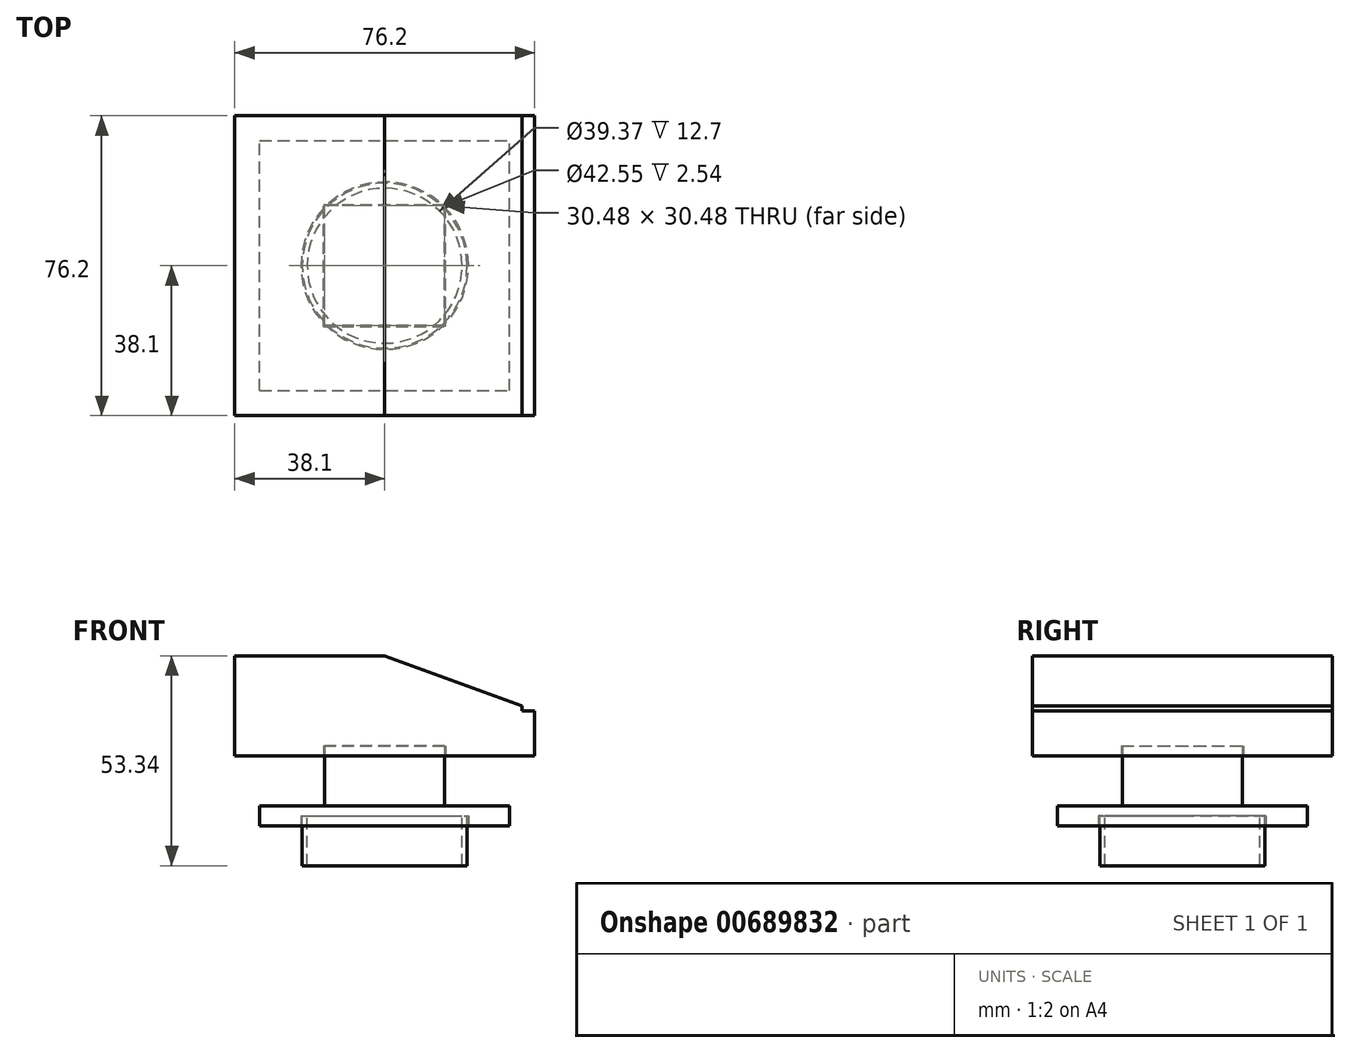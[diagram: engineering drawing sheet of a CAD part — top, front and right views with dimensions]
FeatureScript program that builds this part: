
annotation { "Feature Type Name" : "Feature", "Feature Type Description" : "" }
export const myFeature = defineFeature(function(context is Context, id is Id, definition is map)
    precondition{}
    {
        {
            var Q0;
            Q0=qCreatedBy(makeId("Front.planeOp"),FACE);
            var sketch = newSketch(context, id + "F0", { "sketchPlane" : qUnion([Q0])});
            skLineSegment(sketch, "E0.bottom", {"start": v(-38.1, 0) * mm, "end": v(38.1, 0) * mm});
            skLineSegment(sketch, "E0.top", {"start": v(-38.1, -25.4) * mm, "end": v(38.1, -25.4) * mm});
            skLineSegment(sketch, "E0.left", {"start": v(-38.1, 0) * mm, "end": v(-38.1, -25.4) * mm});
            skLineSegment(sketch, "E0.right", {"start": v(38.1, 0) * mm, "end": v(38.1, -25.4) * mm});
            skSolve(sketch);
        }
        {
            var Q0;
            Q0=qSketchRegion(id+"F0",true);
            extrude(context, id + "F1", {"entities" : qUnion([Q0]), "endBound" : BoundingType.SYMMETRIC, "depth" : 76.2 * mm, "offsetDistance" : 25.4 * mm});
        }
        {
            var Q0;
            Q0=qCreatedBy(makeId("Front.planeOp"),FACE);
            var sketch = newSketch(context, id + "F2", { "sketchPlane" : qUnion([Q0])});
            skLineSegment(sketch, "E1", {"start": v(0, 0) * mm, "end": v(34.93, -12.7) * mm});
            skLineSegment(sketch, "E2", {"start": v(34.93, -12.7) * mm, "end": v(34.93, -13.99) * mm});
            skLineSegment(sketch, "E3", {"start": v(34.93, -13.99) * mm, "end": v(38.1, -13.99) * mm});
            skLineSegment(sketch, "E4", {"start": v(38.1, -13.99) * mm, "end": v(38.1, -25.4) * mm});
            skLineSegment(sketch, "E5", {"start": v(38.1, -25.4) * mm, "end": v(53.54, -25.4) * mm});
            skLineSegment(sketch, "E6", {"start": v(53.54, -25.4) * mm, "end": v(53.54, 0) * mm});
            skLineSegment(sketch, "E7", {"start": v(53.54, 0) * mm, "end": v(0, 0) * mm});
            skSolve(sketch);
        }
        {
            var Q0;
            Q0=qSketchRegion(id+"F2",true);
            extrude(context, id + "F3", {"entities" : qUnion([Q0]), "operationType" : NewBodyOperationType.REMOVE, "endBound" : BoundingType.SYMMETRIC, "oppositeDirection" : true, "depth" : 76.2 * mm, "offsetDistance" : 25.4 * mm});
        }
        {
            var Q0;
            Q0=qCreatedBy(makeId("Front.planeOp"),FACE);
            var sketch = newSketch(context, id + "F4", { "sketchPlane" : qUnion([Q0])});
            skLineSegment(sketch, "E8", {"start": v(0, -1.4) * mm, "end": v(0, -17.06) * mm});
            skSolve(sketch);
        }
        {
            var Q0;
            Q0=makeQuery(id+"F1.opExtrude","SWEPT_FACE",FACE,{"disambiguationData":[OSD([sQuery(id+"F0.wireOp",EDGE,"E0.top")])]});
            var sketch = newSketch(context, id + "F5", { "sketchPlane" : qUnion([Q0])});
            skLineSegment(sketch, "E9.bottom", {"start": v(-15.5, 15.5) * mm, "end": v(15.5, 15.5) * mm});
            skLineSegment(sketch, "E9.top", {"start": v(-15.5, -15.5) * mm, "end": v(15.5, -15.5) * mm});
            skLineSegment(sketch, "E9.left", {"start": v(-15.5, 15.5) * mm, "end": v(-15.5, -15.5) * mm});
            skLineSegment(sketch, "E9.right", {"start": v(15.5, 15.5) * mm, "end": v(15.5, -15.5) * mm});
            skSolve(sketch);
        }
        {
            var Q0;
            Q0=qSketchRegion(id+"F5",true);
            extrude(context, id + "F6", {"entities" : qUnion([Q0]), "operationType" : NewBodyOperationType.REMOVE, "oppositeDirection" : true, "depth" : 2.54 * mm, "offsetDistance" : 25.4 * mm});
        }
        {
            var Q0;
            Q0=qCreatedBy(makeId("Front.planeOp"),FACE);
            var sketch = newSketch(context, id + "F7", { "sketchPlane" : qUnion([Q0])});
            skLineSegment(sketch, "E10.bottom", {"start": v(-31.75, -38.1) * mm, "end": v(31.75, -38.1) * mm});
            skLineSegment(sketch, "E10.top", {"start": v(-31.75, -43.18) * mm, "end": v(31.75, -43.18) * mm});
            skLineSegment(sketch, "E10.left", {"start": v(-31.75, -38.1) * mm, "end": v(-31.75, -43.18) * mm});
            skLineSegment(sketch, "E10.right", {"start": v(31.75, -38.1) * mm, "end": v(31.75, -43.18) * mm});
            skSolve(sketch);
        }
        {
            var Q0;
            Q0=qSketchRegion(id+"F7",true);
            extrude(context, id + "F8", {"entities" : qUnion([Q0]), "endBound" : BoundingType.SYMMETRIC, "depth" : 63.5 * mm, "offsetDistance" : 25.4 * mm});
        }
        {
            var Q0;
            Q0=makeQuery(id+"F8.opExtrude","SWEPT_FACE",FACE,{"disambiguationData":[OSD([sQuery(id+"F7.wireOp",EDGE,"E10.bottom")])]});
            var sketch = newSketch(context, id + "F9", { "sketchPlane" : qUnion([Q0])});
            skLineSegment(sketch, "E11.bottom", {"start": v(-15.24, 15.24) * mm, "end": v(15.24, 15.24) * mm});
            skLineSegment(sketch, "E11.top", {"start": v(-15.24, -15.24) * mm, "end": v(15.24, -15.24) * mm});
            skLineSegment(sketch, "E11.left", {"start": v(-15.24, 15.24) * mm, "end": v(-15.24, -15.24) * mm});
            skLineSegment(sketch, "E11.right", {"start": v(15.24, 15.24) * mm, "end": v(15.24, -15.24) * mm});
            skSolve(sketch);
        }
        {
            var Q0;
            Q0=qSketchRegion(id+"F9",true);
            var Q1;
            Q1=makeQuery(id+"F6.boolean.opBoolean","COPY",FACE,{"derivedFrom":makeQuery(id+"F6.opExtrude","CAP_FACE",FACE,{"disambiguationData":[OSD([sQuery(id+"F5.wireOp",EDGE,"E9.bottom"),sQuery(id+"F5.wireOp",EDGE,"E9.top"),sQuery(id+"F5.wireOp",EDGE,"E9.left"),sQuery(id+"F5.wireOp",EDGE,"E9.right")])],"isStart":false})});
            extrude(context, id + "F10", {"entities" : qUnion([Q0]), "operationType" : NewBodyOperationType.ADD, "endBound" : BoundingType.UP_TO_SURFACE, "depth" : 25.4 * mm, "endBoundEntityFace" : qUnion([Q1]), "offsetDistance" : 25.4 * mm});
        }
        {
            var Q0;
            Q0=makeQuery(id+"F8.opExtrude","SWEPT_FACE",FACE,{"disambiguationData":[OSD([sQuery(id+"F7.wireOp",EDGE,"E10.top")])]});
            var sketch = newSketch(context, id + "F11", { "sketchPlane" : qUnion([Q0])});
            skCircle(sketch, "E12", {"center": v(0, 0) * mm, "radius": 21.27 * mm});
            skSolve(sketch);
        }
        {
            var Q0;
            Q0=qSketchRegion(id+"F11",true);
            extrude(context, id + "F12", {"entities" : qUnion([Q0]), "operationType" : NewBodyOperationType.REMOVE, "oppositeDirection" : true, "depth" : 2.54 * mm, "offsetDistance" : 25.4 * mm});
        }
        {
            var Q0;
            Q0=makeQuery(id+"F12.boolean.opBoolean","COPY",FACE,{"derivedFrom":makeQuery(id+"F12.opExtrude","CAP_FACE",FACE,{"disambiguationData":[OSD([sQuery(id+"F11.wireOp",EDGE,"E12")])],"isStart":false})});
            var sketch = newSketch(context, id + "F13", { "sketchPlane" : qUnion([Q0])});
            skCircle(sketch, "E13", {"center": v(0, 0) * mm, "radius": 20.96 * mm});
            skCircle(sketch, "E14", {"center": v(0, 0) * mm, "radius": 19.69 * mm});
            skSolve(sketch);
        }
        {
            var Q0;
            Q0=qSketchRegion(id+"F13",true);
            extrude(context, id + "F14", {"entities" : qUnion([Q0]), "depth" : 12.7 * mm, "offsetDistance" : 25.4 * mm});
        }
    });
